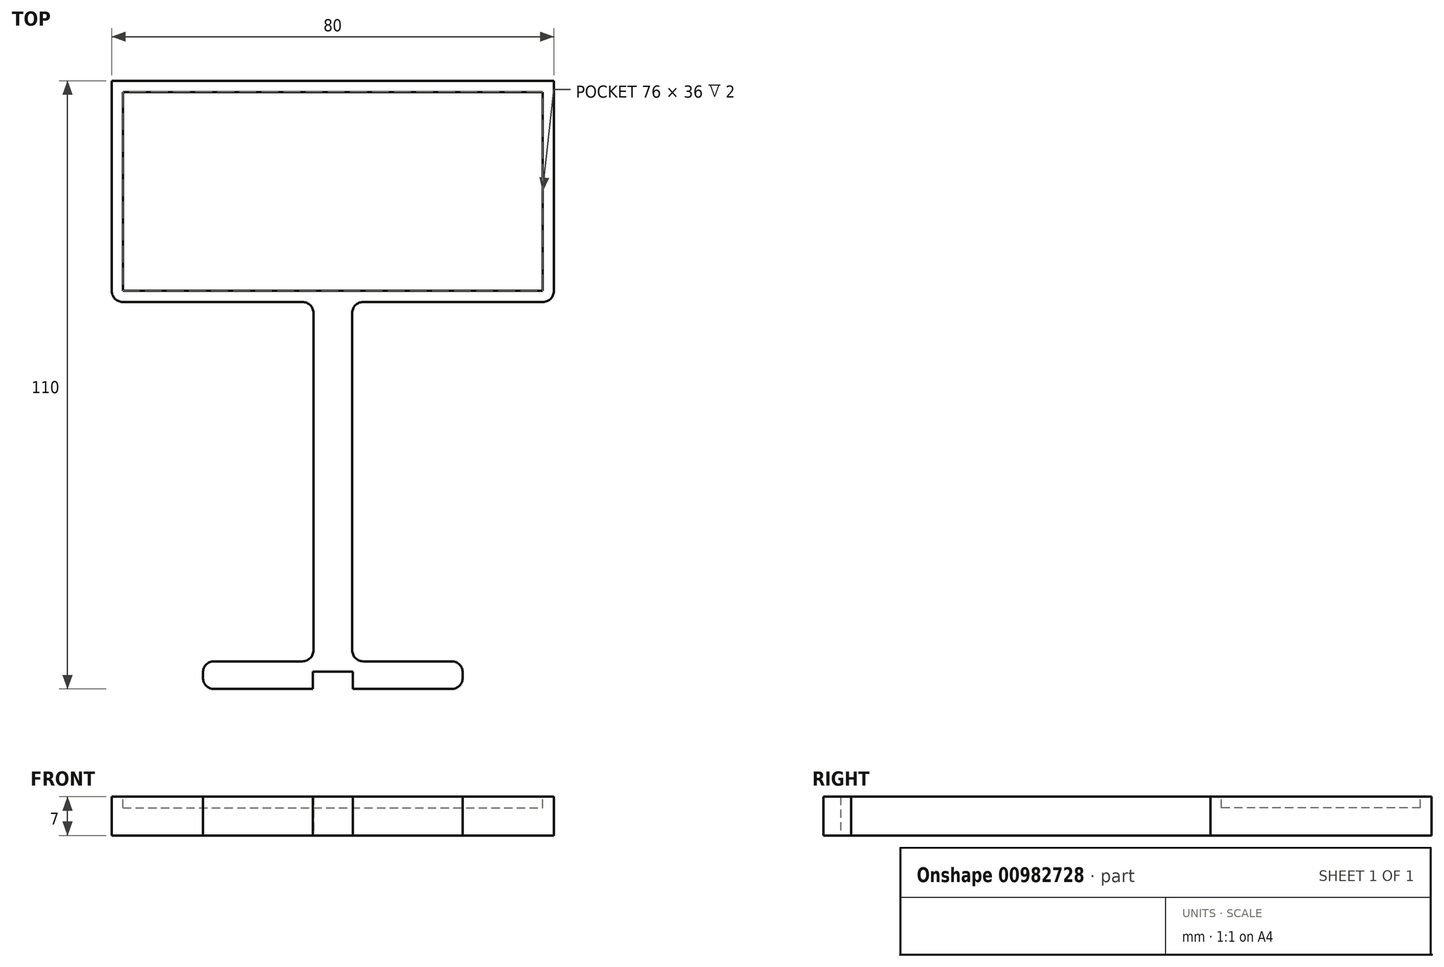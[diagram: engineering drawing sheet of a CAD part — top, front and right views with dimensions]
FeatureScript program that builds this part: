
annotation { "Feature Type Name" : "Feature", "Feature Type Description" : "" }
export const myFeature = defineFeature(function(context is Context, id is Id, definition is map)
    precondition{}
    {
        {
            var Q0;
            Q0=qCreatedBy(makeId("Top.planeOp"),FACE);
            var sketch = newSketch(context, id + "F0", { "sketchPlane" : qUnion([Q0])});
            skLineSegment(sketch, "E0", {"start": v(-40, 0) * mm, "end": v(40, 0) * mm});
            skPoint(sketch, "E1", {"position": v(0, 0) * mm});
            skLineSegment(sketch, "E2", {"start": v(-3.5, 0) * mm, "end": v(-3.5, -65) * mm});
            skLineSegment(sketch, "E3", {"start": v(-3.5, -65) * mm, "end": v(-23.5, -65) * mm});
            skLineSegment(sketch, "E4", {"start": v(-23.5, -65) * mm, "end": v(-23.5, -70) * mm});
            skLineSegment(sketch, "E5", {"start": v(-23.5, -70) * mm, "end": v(23.5, -70) * mm});
            skLineSegment(sketch, "E6", {"start": v(23.5, -70) * mm, "end": v(23.5, -65) * mm});
            skLineSegment(sketch, "E7", {"start": v(23.5, -65) * mm, "end": v(3.5, -65) * mm});
            skLineSegment(sketch, "E8", {"start": v(3.5, -65) * mm, "end": v(3.5, 0) * mm});
            skLineSegment(sketch, "E9.bottom", {"start": v(3.6, -70) * mm, "end": v(-3.6, -70) * mm});
            skLineSegment(sketch, "E9.top", {"start": v(3.6, -66.9) * mm, "end": v(-3.6, -66.9) * mm});
            skLineSegment(sketch, "E9.left", {"start": v(3.6, -70) * mm, "end": v(3.6, -66.9) * mm});
            skLineSegment(sketch, "E9.right", {"start": v(-3.6, -70) * mm, "end": v(-3.6, -66.9) * mm});
            skPoint(sketch, "E9.middle", {"position": v(0, -68.45) * mm});
            skLineSegment(sketch, "E10.bottom", {"start": v(-23.5, -70) * mm, "end": v(-17.5, -70) * mm});
            skLineSegment(sketch, "E10.top", {"start": v(-23.5, -70.3) * mm, "end": v(-17.5, -70.3) * mm});
            skLineSegment(sketch, "E10.left", {"start": v(-23.5, -70) * mm, "end": v(-23.5, -70.3) * mm});
            skLineSegment(sketch, "E10.right", {"start": v(-17.5, -70) * mm, "end": v(-17.5, -70.3) * mm});
            skLineSegment(sketch, "E11.MirrorCS", {"start": v(23.5, -70) * mm, "end": v(17.5, -70) * mm});
            skLineSegment(sketch, "E12.MirrorCS", {"start": v(17.5, -70) * mm, "end": v(17.5, -70.3) * mm});
            skLineSegment(sketch, "E13.MirrorCS", {"start": v(23.5, -70.3) * mm, "end": v(17.5, -70.3) * mm});
            skLineSegment(sketch, "E14.MirrorCS", {"start": v(23.5, -70) * mm, "end": v(23.5, -70.3) * mm});
            skLineSegment(sketch, "E15", {"start": v(-40, 0) * mm, "end": v(-40, 40) * mm});
            skLineSegment(sketch, "E16", {"start": v(-40, 40) * mm, "end": v(40, 40) * mm});
            skLineSegment(sketch, "E17", {"start": v(40, 40) * mm, "end": v(40, 0) * mm});
            skSolve(sketch);
        }
        {
            var Q0;
            {var subQ0=sQuery(id+"F0.wireOp",EDGE,"im0v1Rov-prSM-cwdN-f0IW-ScqFdnQkXUSi");Q0=makeQuery(id+"F0.imprint","IMPRINT",FACE,{"disambiguationData":[TD([[makeQuery(id+"F0.imprint","IMPRINT",EDGE,{"derivedFrom":subQ0}),1.0]])]});}
            var Q1;
            {var subQ7=sQuery(id+"F0.wireOp",EDGE,"E2");Q1=makeQuery(id+"F0.imprint","IMPRINT",FACE,{"disambiguationData":[TD([[makeQuery(id+"F0.imprint","IMPRINT",EDGE,{"derivedFrom":subQ7}),1.0]])]});}
            var Q2;
            Q2=makeQuery(id+"F0.imprint","IMPRINT",FACE,{"disambiguationData":[TD([[makeQuery(id+"F0.imprint","IMPRINT",EDGE,{"derivedFrom":sQuery(id+"F0.wireOp",EDGE,"E10.bottom")}),-1.0]])]});
            var Q3;
            Q3=makeQuery(id+"F0.imprint","IMPRINT",FACE,{"disambiguationData":[TD([[makeQuery(id+"F0.imprint","IMPRINT",EDGE,{"derivedFrom":sQuery(id+"F0.wireOp",EDGE,"E11.MirrorCS")}),1.0]])]});
            var Q4;
            {var subQ0=sQuery(id+"F0.wireOp",EDGE,"E15");Q4=makeQuery(id+"F0.imprint","IMPRINT",FACE,{"disambiguationData":[TD([[makeQuery(id+"F0.imprint","IMPRINT",EDGE,{"derivedFrom":subQ0}),-1.0]])]});}
            extrude(context, id + "F1", {"entities" : qUnion([Q0, Q1, Q2, Q3, Q4]), "depth" : 7 * mm, "offsetDistance" : 25 * mm});
        }
        {
            var Q0;
            Q0=makeQuery(id+"F1.opExtrude","CAP_FACE",FACE,{"disambiguationData":[OSD([sQuery(id+"F0.wireOp",EDGE,"E0"),sQuery(id+"F0.wireOp",EDGE,"im0v1Rov-prSM-cwdN-f0IW-ScqFdnQkXUSi"),sQuery(id+"F0.wireOp",EDGE,"IfBi3EXo-PReU-dRJG-joro-0UU4bWJMkuGZ")])],"isStart":false});
            var sketch = newSketch(context, id + "F2", { "sketchPlane" : qUnion([Q0])});
            skLineSegment(sketch, "E18.bottom", {"start": v(-38, 38) * mm, "end": v(38, 38) * mm});
            skLineSegment(sketch, "E18.top", {"start": v(-38, 2) * mm, "end": v(38, 2) * mm});
            skLineSegment(sketch, "E18.left", {"start": v(-38, 38) * mm, "end": v(-38, 2) * mm});
            skLineSegment(sketch, "E18.right", {"start": v(38, 38) * mm, "end": v(38, 2) * mm});
            skSolve(sketch);
        }
        {
            var Q0;
            Q0=makeQuery(id+"F2.imprint","IMPRINT",FACE,{"disambiguationData":[TD([[makeQuery(id+"F2.imprint","IMPRINT",EDGE,{"derivedFrom":sQuery(id+"F2.wireOp",EDGE,"ba8ffd8e-d2a9-49c5-bc2b-62a2f1bfac4f.sketch_text.stroke-0")}),1.0]])]});
            var Q1;
            Q1=makeQuery(id+"F2.imprint","IMPRINT",FACE,{"disambiguationData":[TD([[makeQuery(id+"F2.imprint","IMPRINT",EDGE,{"derivedFrom":sQuery(id+"F2.wireOp",EDGE,"eUnm1Ftm-mGY1-vFZc-uw5d-RwZqvqndYBnG")}),-1.0]])]});
            var Q2;
            Q2=makeQuery(id+"F2.imprint","IMPRINT",FACE,{"disambiguationData":[TD([[makeQuery(id+"F2.imprint","IMPRINT",EDGE,{"derivedFrom":sQuery(id+"F2.wireOp",EDGE,"E18.bottom")}),-1.0]])]});
            extrude(context, id + "F3", {"entities" : qUnion([Q0, Q1, Q2]), "operationType" : NewBodyOperationType.REMOVE, "oppositeDirection" : true, "depth" : 2 * mm, "offsetDistance" : 25 * mm});
        }
        {
            var Q0;
            Q0=makeQuery(id+"F1.opExtrude","SWEPT_EDGE",EDGE,{"disambiguationData":[OSD([sQuery(id+"F0.wireOp",EDGE,"E0"),sQuery(id+"F0.wireOp",EDGE,"E2")])]});
            var Q1;
            Q1=makeQuery(id+"F1.opExtrude","SWEPT_EDGE",EDGE,{"disambiguationData":[OSD([sQuery(id+"F0.wireOp",EDGE,"E0"),sQuery(id+"F0.wireOp",EDGE,"E8")])]});
            var Q2;
            Q2=makeQuery(id+"F1.opExtrude","SWEPT_EDGE",EDGE,{"disambiguationData":[OSD([sQuery(id+"F0.wireOp",EDGE,"E0"),sQuery(id+"F0.wireOp",EDGE,"im0v1Rov-prSM-cwdN-f0IW-ScqFdnQkXUSi")])]});
            var Q3;
            Q3=makeQuery(id+"F1.opExtrude","SWEPT_EDGE",EDGE,{"disambiguationData":[OSD([sQuery(id+"F0.wireOp",EDGE,"E0"),sQuery(id+"F0.wireOp",EDGE,"IfBi3EXo-PReU-dRJG-joro-0UU4bWJMkuGZ")])]});
            var Q4;
            Q4=makeQuery(id+"F1.opExtrude","SWEPT_EDGE",EDGE,{"disambiguationData":[OSD([sQuery(id+"F0.wireOp",EDGE,"im0v1Rov-prSM-cwdN-f0IW-ScqFdnQkXUSi"),sQuery(id+"F0.wireOp",EDGE,"IfBi3EXo-PReU-dRJG-joro-0UU4bWJMkuGZ")])]});
            var Q5;
            Q5=makeQuery(id+"F1.opExtrude","SWEPT_EDGE",EDGE,{"disambiguationData":[OSD([sQuery(id+"F0.wireOp",EDGE,"E7"),sQuery(id+"F0.wireOp",EDGE,"E8")])]});
            var Q6;
            Q6=makeQuery(id+"F1.opExtrude","SWEPT_EDGE",EDGE,{"disambiguationData":[OSD([sQuery(id+"F0.wireOp",EDGE,"E2"),sQuery(id+"F0.wireOp",EDGE,"E3")])]});
            var Q7;
            Q7=makeQuery(id+"F1.opExtrude","SWEPT_EDGE",EDGE,{"disambiguationData":[OSD([sQuery(id+"F0.wireOp",EDGE,"E3"),sQuery(id+"F0.wireOp",EDGE,"E4")])]});
            var Q8;
            Q8=makeQuery(id+"F1.opExtrude","SWEPT_EDGE",EDGE,{"disambiguationData":[OSD([sQuery(id+"F0.wireOp",EDGE,"E6"),sQuery(id+"F0.wireOp",EDGE,"E7")])]});
            var Q9;
            Q9=makeQuery(id+"F1.opExtrude","SWEPT_EDGE",EDGE,{"disambiguationData":[OSD([sQuery(id+"F0.wireOp",EDGE,"E10.top"),sQuery(id+"F0.wireOp",EDGE,"E10.left")])]});
            var Q10;
            Q10=makeQuery(id+"F1.opExtrude","SWEPT_EDGE",EDGE,{"disambiguationData":[OSD([sQuery(id+"F0.wireOp",EDGE,"E13.MirrorCS"),sQuery(id+"F0.wireOp",EDGE,"E14.MirrorCS")])]});
            fillet(context, id + "F4", {"entities" : qUnion([Q0, Q1, Q2, Q3, Q4, Q5, Q6, Q7, Q8, Q9, Q10]), "radius" : 2 * mm, "tangentPropagation" : true, "allowEdgeOverflow" : false});
        }
    });
